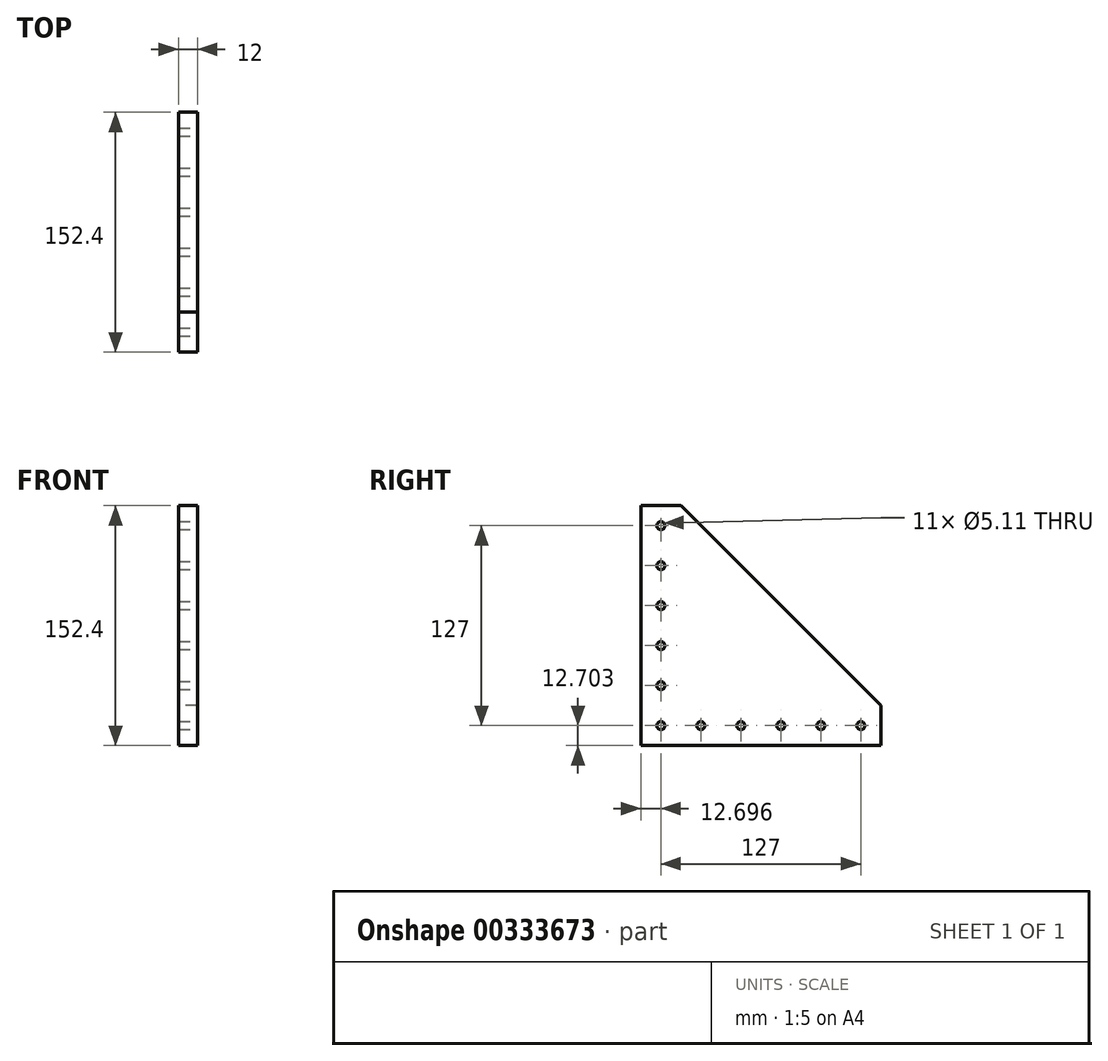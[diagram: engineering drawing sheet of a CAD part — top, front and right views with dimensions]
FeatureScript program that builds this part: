
annotation { "Feature Type Name" : "Feature", "Feature Type Description" : "" }
export const myFeature = defineFeature(function(context is Context, id is Id, definition is map)
    precondition{}
    {
        {
            var Q0;
            Q0=qCreatedBy(makeId("Right.planeOp"),FACE);
            var sketch = newSketch(context, id + "F0", { "sketchPlane" : qUnion([Q0])});
            skLineSegment(sketch, "E0", {"start": v(-89.21, 83.58) * mm, "end": v(-89.21, -68.82) * mm});
            skLineSegment(sketch, "E1", {"start": v(-89.21, -68.82) * mm, "end": v(63.19, -68.82) * mm});
            skLineSegment(sketch, "E2", {"start": v(63.19, -68.82) * mm, "end": v(63.19, -43.42) * mm});
            skLineSegment(sketch, "E3", {"start": v(63.19, -43.42) * mm, "end": v(-63.81, 83.58) * mm});
            skLineSegment(sketch, "E4", {"start": v(-63.81, 83.58) * mm, "end": v(-89.21, 83.58) * mm});
            skSolve(sketch);
        }
        {
            var Q0;
            Q0=makeQuery(id+"F0.imprint","IMPRINT",FACE,{"disambiguationData":[TD([[makeQuery(id+"F0.imprint","IMPRINT",EDGE,{"derivedFrom":sQuery(id+"F0.wireOp",EDGE,"E0")}),1.0]])]});
            extrude(context, id + "F1", {"entities" : qUnion([Q0]), "depth" : 12 * mm});
        }
        {
            var Q0;
            Q0=makeQuery(id+"F1.opExtrude","CAP_FACE",FACE,{"disambiguationData":[OSD([sQuery(id+"F0.wireOp",EDGE,"E0"),sQuery(id+"F0.wireOp",EDGE,"E1"),sQuery(id+"F0.wireOp",EDGE,"E2"),sQuery(id+"F0.wireOp",EDGE,"E3"),sQuery(id+"F0.wireOp",EDGE,"E4")])],"isStart":false});
            var sketch = newSketch(context, id + "F2", { "sketchPlane" : qUnion([Q0])});
            skCircle(sketch, "E5", {"center": v(-76.51, -56.12) * mm, "radius": 2.55 * mm});
            skCircle(sketch, "E6.0.1.0", {"center": v(-76.51, -30.72) * mm, "radius": 2.55 * mm});
            skCircle(sketch, "E6.0.2.0", {"center": v(-76.51, -5.32) * mm, "radius": 2.55 * mm});
            skCircle(sketch, "E6.0.3.0", {"center": v(-76.51, 20.08) * mm, "radius": 2.55 * mm});
            skCircle(sketch, "E6.0.4.0", {"center": v(-76.51, 45.48) * mm, "radius": 2.55 * mm});
            skCircle(sketch, "E6.0.5.0", {"center": v(-76.51, 70.88) * mm, "radius": 2.55 * mm});
            skCircle(sketch, "E6.1.0.0", {"center": v(-51.11, -56.12) * mm, "radius": 2.55 * mm});
            skCircle(sketch, "E6.2.0.0", {"center": v(-25.71, -56.12) * mm, "radius": 2.55 * mm});
            skCircle(sketch, "E6.3.0.0", {"center": v(-0.31, -56.12) * mm, "radius": 2.55 * mm});
            skCircle(sketch, "E6.4.0.0", {"center": v(25.09, -56.12) * mm, "radius": 2.55 * mm});
            skCircle(sketch, "E6.5.0.0", {"center": v(50.49, -56.12) * mm, "radius": 2.55 * mm});
            skLineSegment(sketch, "E6.direction1", {"start": v(-76.51, -56.12) * mm, "end": v(-51.11, -56.12) * mm, "construction": true});
            skLineSegment(sketch, "E6.direction2", {"start": v(-76.51, -56.12) * mm, "end": v(-76.51, -30.72) * mm, "construction": true});
            skSolve(sketch);
        }
        {
            var Q0;
            Q0 = qSketchRegion(id + "F2", true);
            extrude(context, id + "F3", {"entities" : qUnion([Q0]), "operationType" : NewBodyOperationType.REMOVE, "oppositeDirection" : true, "depth" : 25.4 * mm});
        }
    });
